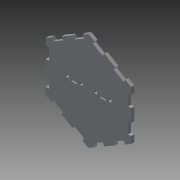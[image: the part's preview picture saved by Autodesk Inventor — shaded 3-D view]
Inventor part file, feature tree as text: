
AUTODESK INVENTOR PART (.ipt)
format: ipt  version: 2015 (Build 190159000, 159)  size: 179,200 bytes
history: native  units: mm
features: extrude x3, sketch x3
ambient origin geometry x8: Origin, YZ Plane, XZ Plane, XY Plane, X Axis, Y Axis, Z Axis, Center Point
bodies: Solid1 (feature_tree)
feature tree (6):
  extrude  "Extrusion1"  Depth=5.5mm
  extrude  "Extrusion2"  Depth=20.0mm
  extrude  "Extrusion3"  Depth=60.0mm TaperAngle=360.0deg
  sketch  "Sketch1"  dims[d4=150.0mm d6=86.60254mm d7=5.5mm]
  sketch  "Sketch2"  dims[d8=180.0deg d9=20.0mm]
  sketch  "Sketch4"  dims[d10=20.0mm d11=60.0mm d13=360.0deg d15=5.5mm d16=0.0mm d17=10.0mm d18=2.0mm d19=10.0mm d20=10.0mm d21=0.0mm d22=20.0mm d23=20.0mm d24=5.0mm d25=5.5mm d26=5.0mm d27=5.5mm d28=10.0mm d29=0.0mm]
